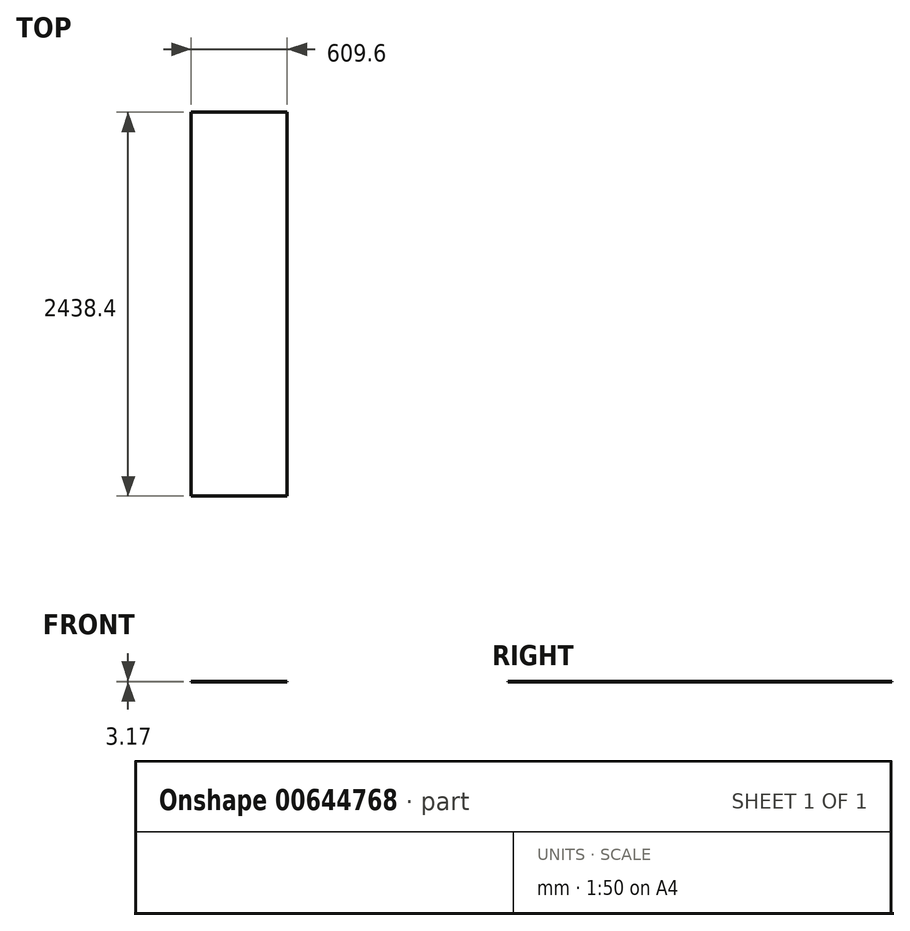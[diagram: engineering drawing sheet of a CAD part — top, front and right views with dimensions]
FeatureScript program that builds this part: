
annotation { "Feature Type Name" : "Feature", "Feature Type Description" : "" }
export const myFeature = defineFeature(function(context is Context, id is Id, definition is map)
    precondition{}
    {
        {
            var Q0;
            Q0=qCreatedBy(makeId("Top.planeOp"),FACE);
            var sketch = newSketch(context, id + "F0", { "sketchPlane" : qUnion([Q0])});
            skLineSegment(sketch, "E0.bottom", {"start": v(0, 0) * mm, "end": v(609.6, 0) * mm});
            skLineSegment(sketch, "E0.top", {"start": v(0, 2438.4) * mm, "end": v(609.6, 2438.4) * mm});
            skLineSegment(sketch, "E0.left", {"start": v(0, 0) * mm, "end": v(0, 2438.4) * mm});
            skLineSegment(sketch, "E0.right", {"start": v(609.6, 0) * mm, "end": v(609.6, 2438.4) * mm});
            skSolve(sketch);
        }
        {
            var Q0;
            Q0=makeQuery(id+"F0.imprint","IMPRINT",FACE,{"disambiguationData":[TD([[makeQuery(id+"F0.imprint","IMPRINT",EDGE,{"derivedFrom":sQuery(id+"F0.wireOp",EDGE,"E0.bottom")}),1.0]])]});
            extrude(context, id + "F1", {"entities" : qUnion([Q0]), "depth" : 3.17 * mm, "offsetDistance" : 25.4 * mm});
        }
    });
